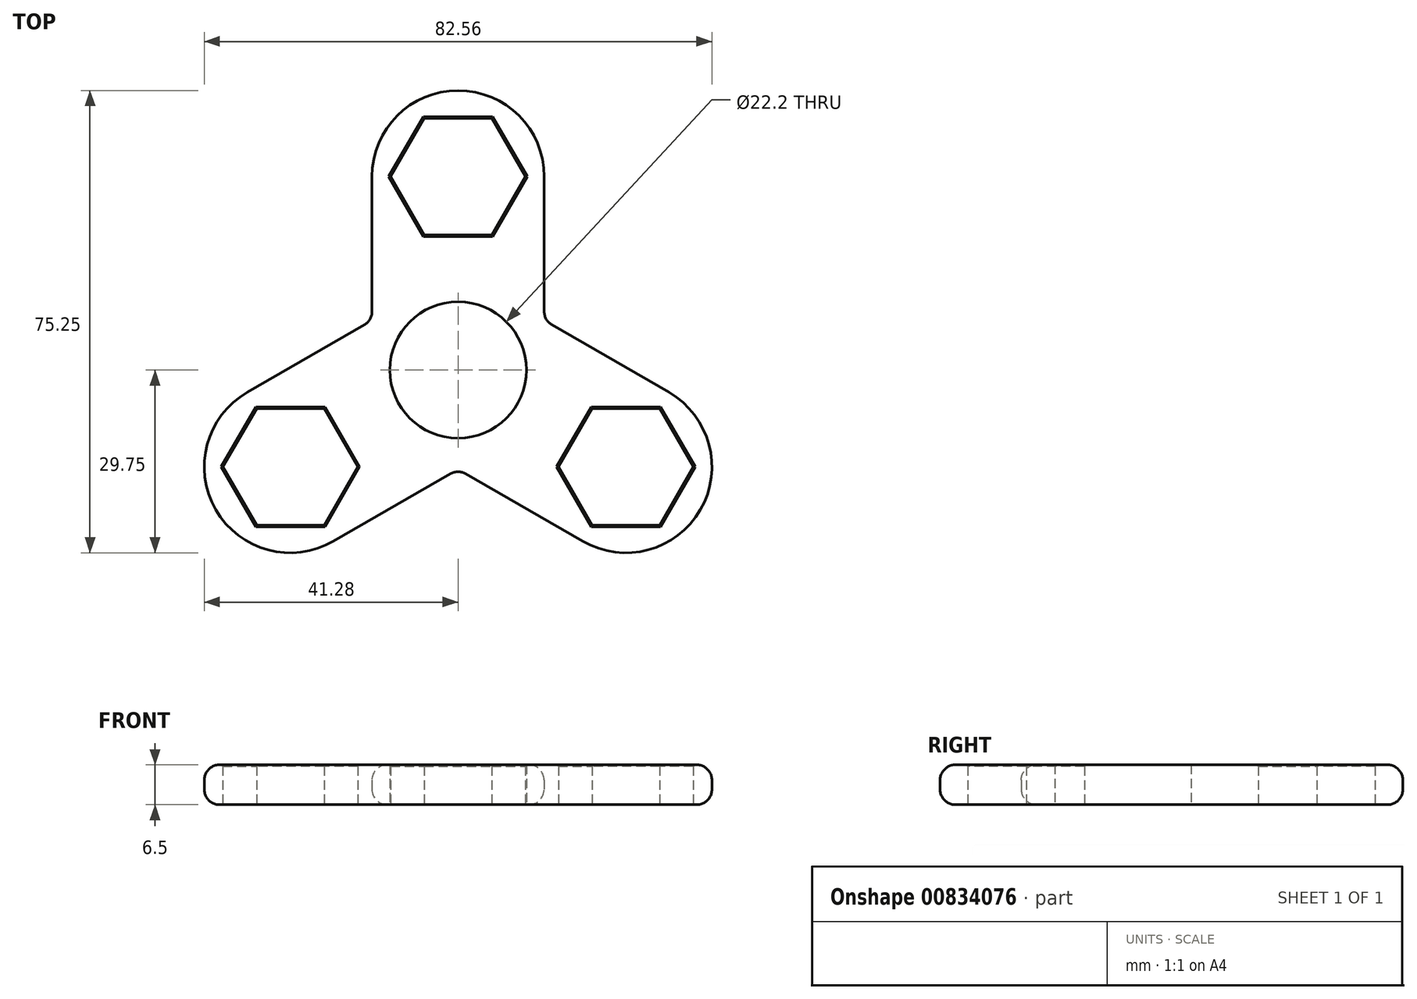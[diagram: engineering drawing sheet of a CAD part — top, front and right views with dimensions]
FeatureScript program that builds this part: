
annotation { "Feature Type Name" : "Feature", "Feature Type Description" : "" }
export const myFeature = defineFeature(function(context is Context, id is Id, definition is map)
    precondition{}
    {
        {
            var Q0;
            Q0=qCreatedBy(makeId("Top.planeOp"),FACE);
            var sketch = newSketch(context, id + "F0", { "sketchPlane" : qUnion([Q0])});
            skCircle(sketch, "E0", {"center": v(0, 0) * mm, "radius": 11.1 * mm});
            skCircle(sketch, "E1", {"center": v(0, 0) * mm, "radius": 14 * mm});
            skCircle(sketch, "E2.cCircle", {"center": v(0, 31.5) * mm, "radius": 9.5 * mm, "construction": true});
            skLineSegment(sketch, "E2.0", {"start": v(5.48, 22) * mm, "end": v(-5.48, 22) * mm});
            skLineSegment(sketch, "E2.1", {"start": v(-5.48, 22) * mm, "end": v(-10.97, 31.5) * mm});
            skLineSegment(sketch, "E2.2", {"start": v(-10.97, 31.5) * mm, "end": v(-5.48, 41) * mm});
            skLineSegment(sketch, "E2.3", {"start": v(-5.48, 41) * mm, "end": v(5.48, 41) * mm});
            skLineSegment(sketch, "E2.4", {"start": v(5.48, 41) * mm, "end": v(10.97, 31.5) * mm});
            skLineSegment(sketch, "E2.5", {"start": v(10.97, 31.5) * mm, "end": v(5.48, 22) * mm});
            skPoint(sketch, "E2.0.midPoint", {"position": v(0, 22) * mm});
            skCircle(sketch, "E3", {"center": v(0, 31.5) * mm, "radius": 14 * mm});
            skLineSegment(sketch, "E4", {"start": v(-14, 31.5) * mm, "end": v(-14, 0) * mm});
            skLineSegment(sketch, "E5.MirrorCS", {"start": v(14, 31.5) * mm, "end": v(14, 0) * mm});
            skLineSegment(sketch, "E6.1.0", {"start": v(-16.31, -15.75) * mm, "end": v(-21.8, -25.25) * mm});
            skCircle(sketch, "E6.1.1", {"center": v(-27.28, -15.75) * mm, "radius": 14 * mm});
            skLineSegment(sketch, "E6.1.2", {"start": v(-20.28, -27.87) * mm, "end": v(7, -12.12) * mm});
            skLineSegment(sketch, "E6.1.3", {"start": v(-34.28, -3.63) * mm, "end": v(-7, 12.12) * mm});
            skLineSegment(sketch, "E6.1.4", {"start": v(-32.76, -6.25) * mm, "end": v(-21.8, -6.25) * mm});
            skLineSegment(sketch, "E6.1.5", {"start": v(-21.8, -6.25) * mm, "end": v(-16.31, -15.75) * mm});
            skLineSegment(sketch, "E6.1.6", {"start": v(-38.25, -15.75) * mm, "end": v(-32.76, -6.25) * mm});
            skLineSegment(sketch, "E6.1.7", {"start": v(-32.76, -25.25) * mm, "end": v(-38.25, -15.75) * mm});
            skLineSegment(sketch, "E6.1.8", {"start": v(-21.8, -25.25) * mm, "end": v(-32.76, -25.25) * mm});
            skLineSegment(sketch, "E6.2.0", {"start": v(21.8, -6.25) * mm, "end": v(32.76, -6.25) * mm});
            skCircle(sketch, "E6.2.1", {"center": v(27.28, -15.75) * mm, "radius": 14 * mm});
            skLineSegment(sketch, "E6.2.2", {"start": v(34.28, -3.63) * mm, "end": v(7, 12.12) * mm});
            skLineSegment(sketch, "E6.2.3", {"start": v(20.28, -27.87) * mm, "end": v(-7, -12.12) * mm});
            skLineSegment(sketch, "E6.2.4", {"start": v(21.8, -25.25) * mm, "end": v(16.31, -15.75) * mm});
            skLineSegment(sketch, "E6.2.5", {"start": v(16.31, -15.75) * mm, "end": v(21.8, -6.25) * mm});
            skLineSegment(sketch, "E6.2.6", {"start": v(32.76, -25.25) * mm, "end": v(21.8, -25.25) * mm});
            skLineSegment(sketch, "E6.2.7", {"start": v(38.25, -15.75) * mm, "end": v(32.76, -25.25) * mm});
            skLineSegment(sketch, "E6.2.8", {"start": v(32.76, -6.25) * mm, "end": v(38.25, -15.75) * mm});
            skSolve(sketch);
        }
        {
            var Q0;
            Q0 = qSketchRegion(id + "F0", true);
            var Q1;
            Q1=makeQuery(id+"F0.imprint","IMPRINT",FACE,{"disambiguationData":[TD([[makeQuery(id+"F0.imprint","IMPRINT",EDGE,{"derivedFrom":sQuery(id+"F0.wireOp",EDGE,"E0")}),-1.0]])]});
            extrude(context, id + "F1", {"entities" : qUnion([Q0, Q1]), "depth" : 6.5 * mm, "offsetDistance" : 25 * mm});
        }
        {
            var Q0;
            Q0=makeQuery(id+"F1.opExtrude","SWEPT_FACE",FACE,{"disambiguationData":[OSD([sQuery(id+"F0.wireOp",EDGE,"E6.1.2")])]});
            var Q1;
            Q1=makeQuery(id+"F1.opExtrude","SWEPT_FACE",FACE,{"disambiguationData":[OSD([sQuery(id+"F0.wireOp",EDGE,"E6.1.1")])]});
            var Q2;
            Q2=makeQuery(id+"F1.opExtrude","SWEPT_FACE",FACE,{"disambiguationData":[OSD([sQuery(id+"F0.wireOp",EDGE,"E6.2.3")])]});
            var Q3;
            Q3=makeQuery(id+"F1.opExtrude","SWEPT_FACE",FACE,{"disambiguationData":[OSD([sQuery(id+"F0.wireOp",EDGE,"E6.2.1")])]});
            var Q4;
            Q4=makeQuery(id+"F1.opExtrude","SWEPT_FACE",FACE,{"disambiguationData":[OSD([sQuery(id+"F0.wireOp",EDGE,"E6.2.2")])]});
            var Q5;
            Q5=makeQuery(id+"F1.opExtrude","SWEPT_FACE",FACE,{"disambiguationData":[OSD([sQuery(id+"F0.wireOp",EDGE,"E5.MirrorCS")])]});
            var Q6;
            Q6=makeQuery(id+"F1.opExtrude","SWEPT_FACE",FACE,{"disambiguationData":[OSD([sQuery(id+"F0.wireOp",EDGE,"E3")])]});
            var Q7;
            Q7=makeQuery(id+"F1.opExtrude","SWEPT_FACE",FACE,{"disambiguationData":[OSD([sQuery(id+"F0.wireOp",EDGE,"E4")])]});
            var Q8;
            Q8=makeQuery(id+"F1.opExtrude","SWEPT_FACE",FACE,{"disambiguationData":[OSD([sQuery(id+"F0.wireOp",EDGE,"E6.1.3")])]});
            fillet(context, id + "F2", {"entities" : qUnion([Q0, Q1, Q2, Q3, Q4, Q5, Q6, Q7, Q8]), "radius" : 2.5 * mm, "tangentPropagation" : true, "allowEdgeOverflow" : false});
        }
        {
            var Q0;
            Q0=makeQuery(id+"F1.opExtrude","CAP_EDGE",EDGE,{"disambiguationData":[OSD([sQuery(id+"F0.wireOp",EDGE,"E6.2.4")])],"isStart":false});
            var Q1;
            Q1=makeQuery(id+"F1.opExtrude","CAP_EDGE",EDGE,{"disambiguationData":[OSD([sQuery(id+"F0.wireOp",EDGE,"E6.2.5")])],"isStart":false});
            var Q2;
            Q2=makeQuery(id+"F1.opExtrude","CAP_EDGE",EDGE,{"disambiguationData":[OSD([sQuery(id+"F0.wireOp",EDGE,"E6.2.0")])],"isStart":false});
            var Q3;
            Q3=makeQuery(id+"F1.opExtrude","CAP_EDGE",EDGE,{"disambiguationData":[OSD([sQuery(id+"F0.wireOp",EDGE,"E6.2.8")])],"isStart":false});
            var Q4;
            Q4=makeQuery(id+"F1.opExtrude","CAP_EDGE",EDGE,{"disambiguationData":[OSD([sQuery(id+"F0.wireOp",EDGE,"E6.2.7")])],"isStart":false});
            var Q5;
            Q5=makeQuery(id+"F1.opExtrude","CAP_EDGE",EDGE,{"disambiguationData":[OSD([sQuery(id+"F0.wireOp",EDGE,"E6.2.6")])],"isStart":false});
            var Q6;
            Q6=makeQuery(id+"F1.opExtrude","CAP_EDGE",EDGE,{"disambiguationData":[OSD([sQuery(id+"F0.wireOp",EDGE,"E6.1.7")])],"isStart":false});
            var Q7;
            Q7=makeQuery(id+"F1.opExtrude","CAP_EDGE",EDGE,{"disambiguationData":[OSD([sQuery(id+"F0.wireOp",EDGE,"E6.1.6")])],"isStart":false});
            var Q8;
            Q8=makeQuery(id+"F1.opExtrude","CAP_EDGE",EDGE,{"disambiguationData":[OSD([sQuery(id+"F0.wireOp",EDGE,"E6.1.4")])],"isStart":false});
            var Q9;
            Q9=makeQuery(id+"F1.opExtrude","CAP_EDGE",EDGE,{"disambiguationData":[OSD([sQuery(id+"F0.wireOp",EDGE,"E6.1.5")])],"isStart":false});
            var Q10;
            Q10=makeQuery(id+"F1.opExtrude","CAP_EDGE",EDGE,{"disambiguationData":[OSD([sQuery(id+"F0.wireOp",EDGE,"E6.1.0")])],"isStart":false});
            var Q11;
            Q11=makeQuery(id+"F1.opExtrude","CAP_EDGE",EDGE,{"disambiguationData":[OSD([sQuery(id+"F0.wireOp",EDGE,"E6.1.8")])],"isStart":false});
            var Q12;
            Q12=makeQuery(id+"F1.opExtrude","CAP_EDGE",EDGE,{"disambiguationData":[OSD([sQuery(id+"F0.wireOp",EDGE,"E2.0")])],"isStart":false});
            var Q13;
            Q13=makeQuery(id+"F1.opExtrude","CAP_EDGE",EDGE,{"disambiguationData":[OSD([sQuery(id+"F0.wireOp",EDGE,"E2.5")])],"isStart":false});
            var Q14;
            Q14=makeQuery(id+"F1.opExtrude","CAP_EDGE",EDGE,{"disambiguationData":[OSD([sQuery(id+"F0.wireOp",EDGE,"E2.4")])],"isStart":false});
            var Q15;
            Q15=makeQuery(id+"F1.opExtrude","CAP_EDGE",EDGE,{"disambiguationData":[OSD([sQuery(id+"F0.wireOp",EDGE,"E2.3")])],"isStart":false});
            var Q16;
            Q16=makeQuery(id+"F1.opExtrude","CAP_EDGE",EDGE,{"disambiguationData":[OSD([sQuery(id+"F0.wireOp",EDGE,"E2.2")])],"isStart":false});
            var Q17;
            Q17=makeQuery(id+"F1.opExtrude","CAP_EDGE",EDGE,{"disambiguationData":[OSD([sQuery(id+"F0.wireOp",EDGE,"E2.1")])],"isStart":false});
            chamfer(context, id + "F3", {"entities" : qUnion([Q0, Q1, Q2, Q3, Q4, Q5, Q6, Q7, Q8, Q9, Q10, Q11, Q12, Q13, Q14, Q15, Q16, Q17]), "width" : 0.25 * mm, "tangentPropagation" : true});
        }
    });
